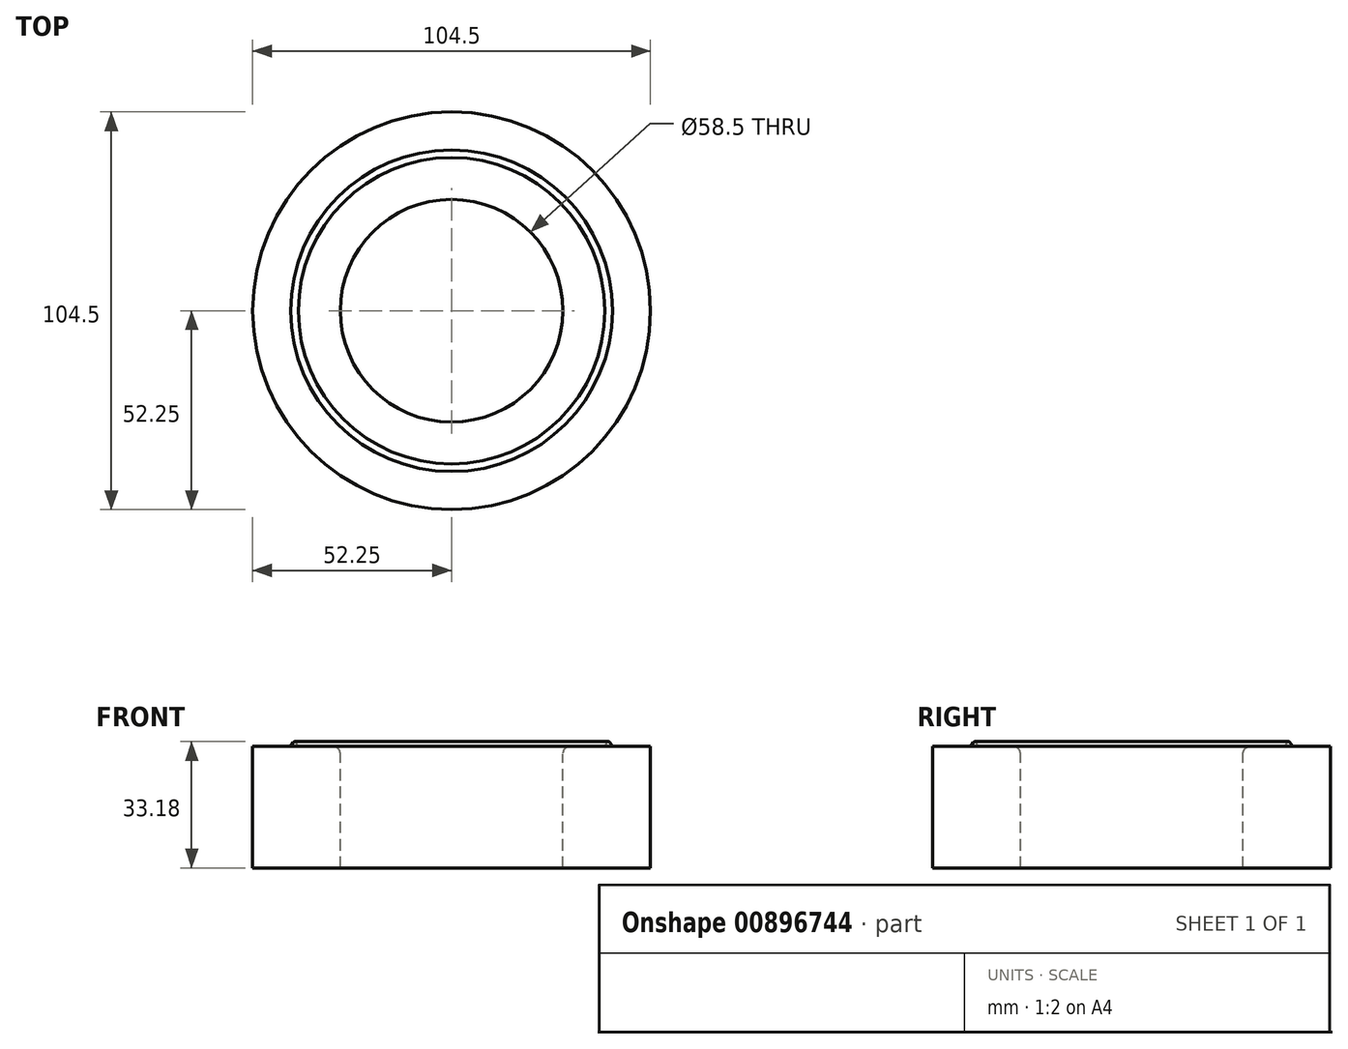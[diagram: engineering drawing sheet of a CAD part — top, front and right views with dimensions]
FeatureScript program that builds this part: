
annotation { "Feature Type Name" : "Feature", "Feature Type Description" : "" }
export const myFeature = defineFeature(function(context is Context, id is Id, definition is map)
    precondition{}
    {
        {
            var Q0;
            Q0=qCreatedBy(makeId("Front.planeOp"),FACE);
            var sketch = newSketch(context, id + "F0", { "sketchPlane" : qUnion([Q0])});
            skLineSegment(sketch, "E0", {"start": v(31.25, 28) * mm, "end": v(40.25, 28) * mm});
            skLineSegment(sketch, "E1", {"start": v(29.25, 26) * mm, "end": v(29.25, 0) * mm});
            skPoint(sketch, "E2.start.orphan", {"position": v(0, 28) * mm});
            skLineSegment(sketch, "E3", {"start": v(0, 28) * mm, "end": v(0, 0) * mm});
            skPoint(sketch, "E4.visualSharp", {"position": v(29.25, 28) * mm});
            skArc(sketch, "E4.filletArc", {"start": v(31.25, 28) * mm, "mid": v(29.84, 27.41) * mm, "end": v(29.25, 26) * mm});
            skLineSegment(sketch, "E5", {"start": v(52.25, 28) * mm, "end": v(42.25, 28) * mm});
            skLineSegment(sketch, "E6", {"start": v(41.58, 29) * mm, "end": v(42.25, 28) * mm});
            skLineSegment(sketch, "E7", {"start": v(40.25, 28) * mm, "end": v(40.92, 29) * mm});
            skLineSegment(sketch, "E8.trimOffspring", {"start": v(44.25, 28) * mm, "end": v(52.25, 28) * mm});
            skPoint(sketch, "E9.visualSharp", {"position": v(41.25, 29.5) * mm});
            skArc(sketch, "E9.filletArc", {"start": v(41.58, 29) * mm, "mid": v(41.25, 29.18) * mm, "end": v(40.92, 29) * mm});
            skLineSegment(sketch, "E10", {"start": v(52.25, 0) * mm, "end": v(52.25, 28) * mm});
            skLineSegment(sketch, "E11", {"start": v(29.25, 0) * mm, "end": v(52.25, 0) * mm});
            skSolve(sketch);
        }
        {
            var Q0;
            Q0 = qSketchRegion(id + "F0", true);
            var Q1;
            Q1=sQuery(id+"F0.wireOp",EDGE,"E3");
            revolve(context, id + "F1", {"surfaceOperationType" : NewSurfaceOperationType.NEW, "entities" : qUnion([Q0]), "axis" : qUnion([Q1]), "revolveType" : RevolveType.FULL});
        }
        {
            var Q0;
            Q0=makeQuery(id+"F1.opRevolve","SWEPT_FACE",FACE,{"disambiguationData":[OSD([sQuery(id+"F0.wireOp",EDGE,"E11")])]});
            var sketch = newSketch(context, id + "F2", { "sketchPlane" : qUnion([Q0])});
            skCircle(sketch, "E12", {"center": v(0, 0) * mm, "radius": 29.25 * mm});
            skCircle(sketch, "E13", {"center": v(0, 0) * mm, "radius": 52.25 * mm});
            skSolve(sketch);
        }
        {
            var Q0;
            Q0 = qSketchRegion(id + "F2", true);
            extrude(context, id + "F3", {"entities" : qUnion([Q0]), "operationType" : NewBodyOperationType.ADD, "depth" : 4 * mm, "offsetDistance" : 25 * mm});
        }
    });
